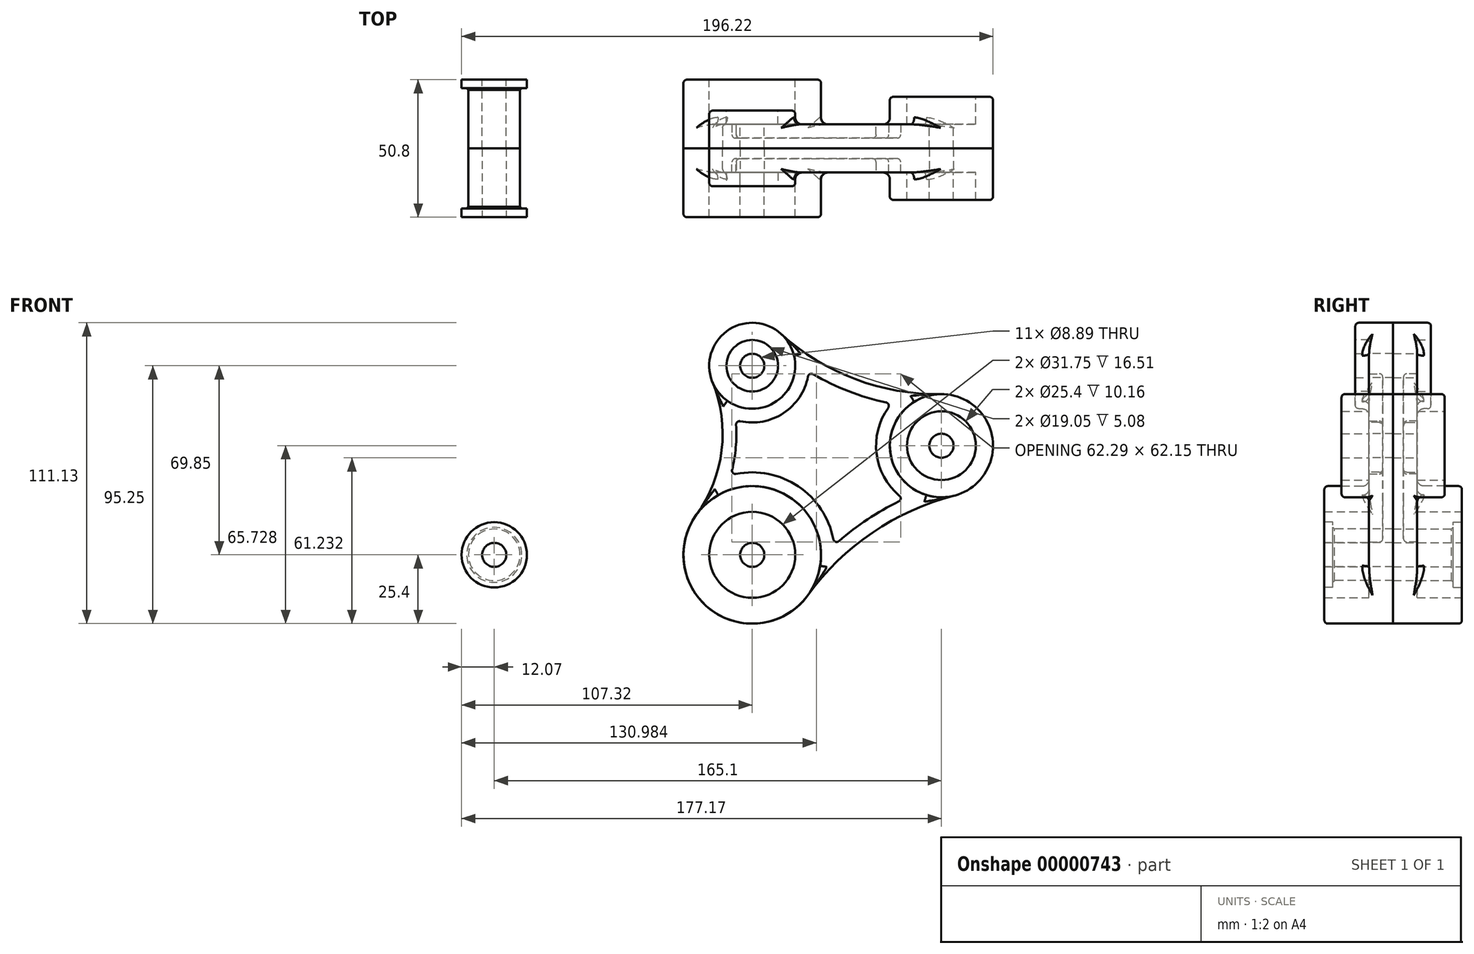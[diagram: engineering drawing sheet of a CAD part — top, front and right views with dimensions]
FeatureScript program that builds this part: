
annotation { "Feature Type Name" : "Feature", "Feature Type Description" : "" }
export const myFeature = defineFeature(function(context is Context, id is Id, definition is map)
    precondition{}
    {
        {
            var Q0;
            Q0=qCreatedBy(makeId("Front.planeOp"),FACE);
            var sketch = newSketch(context, id + "F0", { "sketchPlane" : qUnion([Q0])});
            skCircle(sketch, "E0", {"center": v(0, 0) * mm, "radius": 25.4 * mm});
            skCircle(sketch, "E1", {"center": v(0, 69.85) * mm, "radius": 15.88 * mm});
            skCircle(sketch, "E2", {"center": v(69.85, 40.33) * mm, "radius": 19.05 * mm});
            skLineSegment(sketch, "E3", {"start": v(0, 0) * mm, "end": v(69.85, 40.33) * mm, "construction": true});
            skLineSegment(sketch, "E4", {"start": v(0, 0) * mm, "end": v(74.27, 0) * mm, "construction": true});
            skArc(sketch, "E5", {"start": v(-20.58, 14.89) * mm, "mid": v(-11.3, 38.61) * mm, "end": v(-14.7, 63.85) * mm});
            skArc(sketch, "E6", {"start": v(74.6, 21.88) * mm, "mid": v(44.37, 8.2) * mm, "end": v(20.56, -14.91) * mm});
            skArc(sketch, "E7", {"start": v(10.64, 81.63) * mm, "mid": v(38.02, 64.93) * mm, "end": v(69.6, 59.38) * mm});
            skSolve(sketch);
        }
        {
            var Q0;
            {var subQ0=sQuery(id+"F0.wireOp",EDGE,"E0");var subQ1=sQuery(id+"F0.wireOp",EDGE,"E6");var subQ3=sQuery(id+"F0.wireOp",EDGE,"E5");var subQ4=makeQuery(id+"F0.imprint","INTERSECT",VERTEX,{"derivedFrom":[subQ0,subQ3]});var subQ6=sQuery(id+"F0.wireOp",EDGE,"E1");var subQ9=makeQuery(id+"F0.imprint","INTERSECT",VERTEX,{"derivedFrom":[subQ6,subQ3]});var subQ11=sQuery(id+"F0.wireOp",EDGE,"E2");var subQ13=makeQuery(id+"F0.imprint","INTERSECT",VERTEX,{"derivedFrom":[subQ11,subQ1]});var subQ14=makeQuery(id+"F0.imprint","IMPRINT",EDGE,{"disambiguationData":[TD([[subQ13,1.0]])],"derivedFrom":subQ11});Q0=qUnion([makeQuery(id+"F0.imprint","IMPRINT",FACE,{"disambiguationData":[TD([[makeQuery(id+"F0.imprint","IMPRINT",EDGE,{"disambiguationData":[TD([[subQ4,-1.0]])],"derivedFrom":subQ0}),1.0]])]}),makeQuery(id+"F0.imprint","IMPRINT",FACE,{"disambiguationData":[TD([[makeQuery(id+"F0.imprint","IMPRINT",EDGE,{"disambiguationData":[TD([[subQ9,1.0]])],"derivedFrom":subQ6}),1.0]])]}),makeQuery(id+"F0.imprint","IMPRINT",FACE,{"disambiguationData":[TD([[subQ14,1.0]])]}),makeQuery(id+"F0.imprint","IMPRINT",FACE,{"disambiguationData":[TD([[makeQuery(id+"F0.imprint","IMPRINT",EDGE,{"derivedFrom":subQ3}),-1.0]])]})]);}
            extrude(context, id + "F1", {"entities" : qUnion([Q0]), "depth" : 8.9 * mm});
        }
        {
            var Q0;
            {var subQ0=sQuery(id+"F0.wireOp",EDGE,"E1");var subQ2=makeQuery(id+"F0.imprint","INTERSECT",VERTEX,{"derivedFrom":[subQ0,sQuery(id+"F0.wireOp",EDGE,"E5")]});Q0=makeQuery(id+"F0.imprint","IMPRINT",FACE,{"disambiguationData":[TD([[makeQuery(id+"F0.imprint","IMPRINT",EDGE,{"disambiguationData":[TD([[subQ2,1.0]])],"derivedFrom":subQ0}),1.0]])]});}
            extrude(context, id + "F2", {"entities" : qUnion([Q0]), "operationType" : NewBodyOperationType.ADD, "depth" : 13.97 * mm});
        }
        {
            var Q0;
            {var subQ0=sQuery(id+"F0.wireOp",EDGE,"E2");var subQ2=makeQuery(id+"F0.imprint","INTERSECT",VERTEX,{"derivedFrom":[subQ0,sQuery(id+"F0.wireOp",EDGE,"E6")]});Q0=makeQuery(id+"F0.imprint","IMPRINT",FACE,{"disambiguationData":[TD([[makeQuery(id+"F0.imprint","IMPRINT",EDGE,{"disambiguationData":[TD([[subQ2,1.0]])],"derivedFrom":subQ0}),1.0]])]});}
            extrude(context, id + "F3", {"entities" : qUnion([Q0]), "operationType" : NewBodyOperationType.ADD, "depth" : 19.05 * mm});
        }
        {
            var Q0;
            {var subQ0=sQuery(id+"F0.wireOp",EDGE,"E0");var subQ2=makeQuery(id+"F0.imprint","INTERSECT",VERTEX,{"derivedFrom":[subQ0,sQuery(id+"F0.wireOp",EDGE,"E5")]});Q0=makeQuery(id+"F0.imprint","IMPRINT",FACE,{"disambiguationData":[TD([[makeQuery(id+"F0.imprint","IMPRINT",EDGE,{"disambiguationData":[TD([[subQ2,-1.0]])],"derivedFrom":subQ0}),1.0]])]});}
            extrude(context, id + "F4", {"entities" : qUnion([Q0]), "operationType" : NewBodyOperationType.ADD, "depth" : 25.4 * mm});
        }
        {
            var Q0;
            Q0=makeQuery(id+"F1.opExtrude","CAP_FACE",FACE,{"disambiguationData":[OSD([sQuery(id+"F0.wireOp",EDGE,"E0"),sQuery(id+"F0.wireOp",EDGE,"E1"),sQuery(id+"F0.wireOp",EDGE,"E2"),sQuery(id+"F0.wireOp",EDGE,"E5"),sQuery(id+"F0.wireOp",EDGE,"E6"),sQuery(id+"F0.wireOp",EDGE,"E7")])],"isStart":false});
            var sketch = newSketch(context, id + "F5", { "sketchPlane" : qUnion([Q0])});
            skCircle(sketch, "E8.0", {"center": v(0, 69.85) * mm, "radius": 20.96 * mm});
            skCircle(sketch, "E9.0", {"center": v(69.85, 40.33) * mm, "radius": 24.13 * mm});
            skCircle(sketch, "E10.0", {"center": v(0, 0) * mm, "radius": 30.48 * mm});
            skArc(sketch, "E11.0", {"start": v(-16.46, 11.91) * mm, "mid": v(-6.25, 38) * mm, "end": v(-10, 65.77) * mm});
            skArc(sketch, "E12.0", {"start": v(7.23, 77.86) * mm, "mid": v(36.23, 60.18) * mm, "end": v(69.67, 54.3) * mm});
            skArc(sketch, "E13.0", {"start": v(73.34, 26.8) * mm, "mid": v(41.51, 12.4) * mm, "end": v(16.45, -11.93) * mm});
            skSolve(sketch);
        }
        {
            var Q0;
            {var subQ5=sQuery(id+"F5.wireOp",EDGE,"E12.0");var subQ7=sQuery(id+"F5.wireOp",EDGE,"E8.0");var subQ8=makeQuery(id+"F5.imprint","INTERSECT",VERTEX,{"derivedFrom":[subQ7,subQ5]});Q0=makeQuery(id+"F5.imprint","IMPRINT",FACE,{"disambiguationData":[TD([[makeQuery(id+"F5.imprint","IMPRINT",EDGE,{"disambiguationData":[TD([[subQ8,1.0]])],"derivedFrom":subQ7}),-1.0]])]});}
            extrude(context, id + "F6", {"entities" : qUnion([Q0]), "operationType" : NewBodyOperationType.REMOVE, "oppositeDirection" : true, "depth" : 5.08 * mm});
        }
        {
            var Q0;
            Q0=makeQuery(id+"F4.opExtrude","CAP_FACE",FACE,{"disambiguationData":[OSD([sQuery(id+"F0.wireOp",EDGE,"E0")])],"isStart":false});
            var sketch = newSketch(context, id + "F7", { "sketchPlane" : qUnion([Q0])});
            skCircle(sketch, "E14", {"center": v(0, 0) * mm, "radius": 15.88 * mm});
            skCircle(sketch, "E15.0", {"center": v(0, 69.85) * mm, "radius": 15.88 * mm, "construction": true});
            skCircle(sketch, "E15.1", {"center": v(69.85, 40.33) * mm, "radius": 19.05 * mm, "construction": true});
            skCircle(sketch, "E16", {"center": v(0, 69.85) * mm, "radius": 9.53 * mm});
            skCircle(sketch, "E17", {"center": v(69.85, 40.33) * mm, "radius": 12.7 * mm});
            skSolve(sketch);
        }
        {
            var Q0;
            Q0=makeQuery(id+"F7.imprint","IMPRINT",FACE,{"disambiguationData":[TD([[makeQuery(id+"F7.imprint","IMPRINT",EDGE,{"derivedFrom":sQuery(id+"F7.wireOp",EDGE,"E14")}),1.0]])]});
            var Q1;
            Q1=makeQuery(id+"F7.imprint","IMPRINT",FACE,{"disambiguationData":[TD([[makeQuery(id+"F7.imprint","IMPRINT",EDGE,{"derivedFrom":sQuery(id+"F7.wireOp",EDGE,"E16")}),1.0]])]});
            var Q2;
            Q2=makeQuery(id+"F7.imprint","IMPRINT",FACE,{"disambiguationData":[TD([[makeQuery(id+"F7.imprint","IMPRINT",EDGE,{"derivedFrom":sQuery(id+"F7.wireOp",EDGE,"E17")}),1.0]])]});
            var Q3;
            Q3=makeQuery(id+"F1.opExtrude","CAP_FACE",FACE,{"disambiguationData":[OSD([sQuery(id+"F0.wireOp",EDGE,"E0"),sQuery(id+"F0.wireOp",EDGE,"E1"),sQuery(id+"F0.wireOp",EDGE,"E2"),sQuery(id+"F0.wireOp",EDGE,"E5"),sQuery(id+"F0.wireOp",EDGE,"E6"),sQuery(id+"F0.wireOp",EDGE,"E7")])],"isStart":false});
            extrude(context, id + "F8", {"entities" : qUnion([Q0, Q1, Q2]), "operationType" : NewBodyOperationType.REMOVE, "endBound" : BoundingType.UP_TO_SURFACE, "oppositeDirection" : true, "endBoundEntityFace" : qUnion([Q3]), "depth" : 25.4 * mm});
        }
        {
            var Q0;
            Q0=makeQuery(id+"F8.boolean.opBoolean","COPY",FACE,{"derivedFrom":makeQuery(id+"F8.opExtrude","CAP_FACE",FACE,{"disambiguationData":[OSD([sQuery(id+"F7.wireOp",EDGE,"E17")])],"isStart":false})});
            var sketch = newSketch(context, id + "F9", { "sketchPlane" : qUnion([Q0])});
            skCircle(sketch, "E18.0", {"center": v(0, 69.85) * mm, "radius": 9.53 * mm});
            skCircle(sketch, "E18.1", {"center": v(0, 0) * mm, "radius": 15.88 * mm});
            skCircle(sketch, "E18.2", {"center": v(69.85, 40.33) * mm, "radius": 12.7 * mm});
            skCircle(sketch, "E19", {"center": v(0, 0) * mm, "radius": 4.45 * mm});
            skCircle(sketch, "E20", {"center": v(0, 69.85) * mm, "radius": 4.45 * mm});
            skCircle(sketch, "E21", {"center": v(69.85, 40.33) * mm, "radius": 4.45 * mm});
            skSolve(sketch);
        }
        {
            var Q0;
            Q0=makeQuery(id+"F9.imprint","IMPRINT",FACE,{"disambiguationData":[TD([[makeQuery(id+"F9.imprint","IMPRINT",EDGE,{"derivedFrom":sQuery(id+"F9.wireOp",EDGE,"E20")}),1.0]])]});
            var Q1;
            Q1=makeQuery(id+"F9.imprint","IMPRINT",FACE,{"disambiguationData":[TD([[makeQuery(id+"F9.imprint","IMPRINT",EDGE,{"derivedFrom":sQuery(id+"F9.wireOp",EDGE,"E21")}),1.0]])]});
            var Q2;
            Q2=makeQuery(id+"F9.imprint","IMPRINT",FACE,{"disambiguationData":[TD([[makeQuery(id+"F9.imprint","IMPRINT",EDGE,{"derivedFrom":sQuery(id+"F9.wireOp",EDGE,"E19")}),1.0]])]});
            extrude(context, id + "F10", {"entities" : qUnion([Q0, Q1, Q2]), "operationType" : NewBodyOperationType.REMOVE, "endBound" : BoundingType.THROUGH_ALL, "oppositeDirection" : true, "depth" : 25.4 * mm});
        }
        {
            var Q0;
            Q0=makeQuery(id+"F6.boolean.opBoolean","COPY",FACE,{"derivedFrom":makeQuery(id+"F6.opExtrude","CAP_FACE",FACE,{"disambiguationData":[OSD([sQuery(id+"F5.wireOp",EDGE,"E8.0"),sQuery(id+"F5.wireOp",EDGE,"E9.0"),sQuery(id+"F5.wireOp",EDGE,"E10.0"),sQuery(id+"F5.wireOp",EDGE,"E11.0"),sQuery(id+"F5.wireOp",EDGE,"E12.0"),sQuery(id+"F5.wireOp",EDGE,"E13.0")])],"isStart":false})});
            var Q1;
            Q1=makeQuery(id+"F6.boolean.opBoolean","COPY",EDGE,{"derivedFrom":makeQuery(id+"F6.opExtrude","SWEPT_EDGE",EDGE,{"disambiguationData":[OSD([sQuery(id+"F5.wireOp",EDGE,"E8.0"),sQuery(id+"F5.wireOp",EDGE,"E11.0")])]})});
            var Q2;
            Q2=makeQuery(id+"F6.boolean.opBoolean","COPY",EDGE,{"derivedFrom":makeQuery(id+"F6.opExtrude","SWEPT_EDGE",EDGE,{"disambiguationData":[OSD([sQuery(id+"F5.wireOp",EDGE,"E8.0"),sQuery(id+"F5.wireOp",EDGE,"E12.0")])]})});
            var Q3;
            Q3=makeQuery(id+"F6.boolean.opBoolean","COPY",EDGE,{"derivedFrom":makeQuery(id+"F6.opExtrude","SWEPT_EDGE",EDGE,{"disambiguationData":[OSD([sQuery(id+"F5.wireOp",EDGE,"E9.0"),sQuery(id+"F5.wireOp",EDGE,"E12.0")])]})});
            var Q4;
            Q4=makeQuery(id+"F6.boolean.opBoolean","COPY",EDGE,{"derivedFrom":makeQuery(id+"F6.opExtrude","SWEPT_EDGE",EDGE,{"disambiguationData":[OSD([sQuery(id+"F5.wireOp",EDGE,"E9.0"),sQuery(id+"F5.wireOp",EDGE,"E13.0")])]})});
            var Q5;
            Q5=makeQuery(id+"F6.boolean.opBoolean","COPY",EDGE,{"derivedFrom":makeQuery(id+"F6.opExtrude","SWEPT_EDGE",EDGE,{"disambiguationData":[OSD([sQuery(id+"F5.wireOp",EDGE,"E10.0"),sQuery(id+"F5.wireOp",EDGE,"E13.0")])]})});
            var Q6;
            Q6=makeQuery(id+"F6.boolean.opBoolean","COPY",EDGE,{"derivedFrom":makeQuery(id+"F6.opExtrude","SWEPT_EDGE",EDGE,{"disambiguationData":[OSD([sQuery(id+"F5.wireOp",EDGE,"E10.0"),sQuery(id+"F5.wireOp",EDGE,"E11.0")])]})});
            var Q7;
            Q7=makeQuery(id+"F6.boolean.opBoolean","COPY",EDGE,{"derivedFrom":makeQuery(id+"F6.opExtrude","CAP_EDGE",EDGE,{"disambiguationData":[OSD([sQuery(id+"F5.wireOp",EDGE,"E10.0")])],"isStart":true})});
            var Q8;
            Q8=makeQuery(id+"F1.opExtrude","CAP_EDGE",EDGE,{"disambiguationData":[OSD([sQuery(id+"F0.wireOp",EDGE,"E7")])],"isStart":false});
            var Q9;
            Q9=makeQuery(id+"F1.opExtrude","CAP_EDGE",EDGE,{"disambiguationData":[OSD([sQuery(id+"F0.wireOp",EDGE,"E6")])],"isStart":false});
            var Q10;
            Q10=makeQuery(id+"F1.opExtrude","CAP_EDGE",EDGE,{"disambiguationData":[OSD([sQuery(id+"F0.wireOp",EDGE,"E5")])],"isStart":false});
            var Q11;
            Q11=makeQuery(id+"F4.opExtrude","CAP_EDGE",EDGE,{"disambiguationData":[OSD([sQuery(id+"F0.wireOp",EDGE,"E0")])],"isStart":false});
            var Q12;
            Q12=makeQuery(id+"F3.opExtrude","CAP_EDGE",EDGE,{"disambiguationData":[OSD([sQuery(id+"F0.wireOp",EDGE,"E2")])],"isStart":false});
            var Q13;
            Q13=makeQuery(id+"F2.opExtrude","CAP_EDGE",EDGE,{"disambiguationData":[OSD([sQuery(id+"F0.wireOp",EDGE,"E1")])],"isStart":false});
            fillet(context, id + "F11", {"entities" : qUnion([Q0, Q1, Q2, Q3, Q4, Q5, Q6, Q7, Q8, Q9, Q10, Q11, Q12, Q13]), "radius" : 1.27 * mm, "tangentPropagation" : true, "allowEdgeOverflow" : false});
        }
        {
            var Q0;
            {var subQ0=sQuery(id+"F0.wireOp",EDGE,"E2");Q0=makeQuery(id+"F3.boolean.opBoolean","INTERSECT",EDGE,{"derivedFrom":[makeQuery(id+"F1.opExtrude","CAP_FACE",FACE,{"disambiguationData":[OSD([sQuery(id+"F0.wireOp",EDGE,"E0"),sQuery(id+"F0.wireOp",EDGE,"E1"),subQ0,sQuery(id+"F0.wireOp",EDGE,"E5"),sQuery(id+"F0.wireOp",EDGE,"E6"),sQuery(id+"F0.wireOp",EDGE,"E7")])],"isStart":false}),makeQuery(id+"F3.opExtrude","SWEPT_FACE",FACE,{"disambiguationData":[OSD([subQ0])]})]});}
            var Q1;
            {var subQ0=sQuery(id+"F0.wireOp",EDGE,"E0");Q1=makeQuery(id+"F4.boolean.opBoolean","INTERSECT",EDGE,{"derivedFrom":[makeQuery(id+"F1.opExtrude","CAP_FACE",FACE,{"disambiguationData":[OSD([subQ0,sQuery(id+"F0.wireOp",EDGE,"E1"),sQuery(id+"F0.wireOp",EDGE,"E2"),sQuery(id+"F0.wireOp",EDGE,"E5"),sQuery(id+"F0.wireOp",EDGE,"E6"),sQuery(id+"F0.wireOp",EDGE,"E7")])],"isStart":false}),makeQuery(id+"F4.opExtrude","SWEPT_FACE",FACE,{"disambiguationData":[OSD([subQ0])]})]});}
            var Q2;
            {var subQ0=sQuery(id+"F0.wireOp",EDGE,"E1");Q2=makeQuery(id+"F2.boolean.opBoolean","INTERSECT",EDGE,{"derivedFrom":[makeQuery(id+"F1.opExtrude","CAP_FACE",FACE,{"disambiguationData":[OSD([sQuery(id+"F0.wireOp",EDGE,"E0"),subQ0,sQuery(id+"F0.wireOp",EDGE,"E2"),sQuery(id+"F0.wireOp",EDGE,"E5"),sQuery(id+"F0.wireOp",EDGE,"E6"),sQuery(id+"F0.wireOp",EDGE,"E7")])],"isStart":false}),makeQuery(id+"F2.opExtrude","SWEPT_FACE",FACE,{"disambiguationData":[OSD([subQ0])]})]});}
            fillet(context, id + "F12", {"entities" : qUnion([Q0, Q1, Q2]), "radius" : 2.54 * mm, "tangentPropagation" : true, "allowEdgeOverflow" : false});
        }
        {
            var Q0;
            Q0=makeQuery(id+"F1.opExtrude","SWEPT_BODY",BODY,{"disambiguationData":[OSD([sQuery(id+"F0.wireOp",EDGE,"E0"),sQuery(id+"F0.wireOp",EDGE,"E1"),sQuery(id+"F0.wireOp",EDGE,"E2"),sQuery(id+"F0.wireOp",EDGE,"E5"),sQuery(id+"F0.wireOp",EDGE,"E6"),sQuery(id+"F0.wireOp",EDGE,"E7")])]});
            var Q1;
            Q1=qCreatedBy(makeId("Front.planeOp"),FACE);
            mirror(context, id + "F13", {"entities" : qUnion([Q0]), "mirrorPlane" : qUnion([Q1])});
        }
        {
            var Q0;
            Q0=makeQuery(id+"F8.boolean.opBoolean","COPY",FACE,{"derivedFrom":makeQuery(id+"F8.opExtrude","CAP_FACE",FACE,{"disambiguationData":[OSD([sQuery(id+"F7.wireOp",EDGE,"E16")])],"isStart":false})});
            var sketch = newSketch(context, id + "F14", { "sketchPlane" : qUnion([Q0])});
            skCircle(sketch, "E22.0.0", {"center": v(0, 69.85) * mm, "radius": 9.53 * mm});
            skSolve(sketch);
        }
        {
            var Q0;
            Q0=makeQuery(id+"F14.imprint","IMPRINT",FACE,{"disambiguationData":[TD([[makeQuery(id+"F14.imprint","IMPRINT",EDGE,{"derivedFrom":sQuery(id+"F14.wireOp",EDGE,"E22.0.0")}),-1.0]])]});
            var Q1;
            Q1=makeQuery(id+"F2.opExtrude","CAP_FACE",FACE,{"disambiguationData":[OSD([sQuery(id+"F0.wireOp",EDGE,"E1")])],"isStart":false});
            extrude(context, id + "F15", {"entities" : qUnion([Q0]), "endBound" : BoundingType.UP_TO_SURFACE, "endBoundEntityFace" : qUnion([Q1]), "depth" : 25.4 * mm});
        }
        {
            var Q0;
            Q0=makeQuery(id+"F8.boolean.opBoolean","COPY",FACE,{"derivedFrom":makeQuery(id+"F8.opExtrude","CAP_FACE",FACE,{"disambiguationData":[OSD([sQuery(id+"F7.wireOp",EDGE,"E17")])],"isStart":false})});
            var Q1;
            Q1=makeQuery(id+"F3.opExtrude","CAP_FACE",FACE,{"disambiguationData":[OSD([sQuery(id+"F0.wireOp",EDGE,"E2")])],"isStart":false});
            extrude(context, id + "F16", {"entities" : qUnion([Q0]), "endBound" : BoundingType.UP_TO_SURFACE, "endBoundEntityFace" : qUnion([Q1]), "depth" : 25.4 * mm});
        }
        {
            var Q0;
            Q0=makeQuery(id+"F8.boolean.opBoolean","COPY",FACE,{"derivedFrom":makeQuery(id+"F8.opExtrude","CAP_FACE",FACE,{"disambiguationData":[OSD([sQuery(id+"F7.wireOp",EDGE,"E14")])],"isStart":false})});
            var sketch = newSketch(context, id + "F17", { "sketchPlane" : qUnion([Q0])});
            skCircle(sketch, "E23.0", {"center": v(0, 0) * mm, "radius": 4.45 * mm});
            skCircle(sketch, "E23.1", {"center": v(0, 0) * mm, "radius": 15.88 * mm});
            skSolve(sketch);
        }
        {
            var Q0;
            Q0=makeQuery(id+"F17.imprint","IMPRINT",FACE,{"disambiguationData":[TD([[makeQuery(id+"F17.imprint","IMPRINT",EDGE,{"derivedFrom":sQuery(id+"F17.wireOp",EDGE,"E23.0")}),-1.0]])]});
            var Q1;
            Q1=makeQuery(id+"F4.opExtrude","CAP_FACE",FACE,{"disambiguationData":[OSD([sQuery(id+"F0.wireOp",EDGE,"E0")])],"isStart":false});
            extrude(context, id + "F18", {"entities" : qUnion([Q0]), "endBound" : BoundingType.UP_TO_SURFACE, "endBoundEntityFace" : qUnion([Q1]), "depth" : 25.4 * mm});
        }
        {
            var Q0;
            Q0=qCreatedBy(makeId("Top.planeOp"),FACE);
            var sketch = newSketch(context, id + "F19", { "sketchPlane" : qUnion([Q0])});
            skLineSegment(sketch, "E24", {"start": v(-90.8, 0) * mm, "end": v(-90.8, -25.4) * mm});
            skLineSegment(sketch, "E25", {"start": v(-90.8, -25.4) * mm, "end": v(-83.19, -25.4) * mm});
            skLineSegment(sketch, "E26", {"start": v(-83.19, -25.4) * mm, "end": v(-83.19, -22.23) * mm});
            skLineSegment(sketch, "E27", {"start": v(-83.19, -22.23) * mm, "end": v(-85.1, -22.23) * mm});
            skLineSegment(sketch, "E28", {"start": v(-85.1, -22.23) * mm, "end": v(-85.73, -21.6) * mm});
            skLineSegment(sketch, "E29", {"start": v(-85.73, -21.6) * mm, "end": v(-85.73, 0) * mm});
            skLineSegment(sketch, "E30", {"start": v(-85.73, 0) * mm, "end": v(-90.8, 0) * mm});
            skLineSegment(sketch, "E31.0", {"start": v(24.13, -25.4) * mm, "end": v(-24.13, -25.4) * mm});
            skLineSegment(sketch, "E32", {"start": v(-95.25, -25.4) * mm, "end": v(-95.25, 0) * mm, "construction": true});
            skSolve(sketch);
        }
        {
            var Q0;
            Q0=makeQuery(id+"F19.imprint","IMPRINT",FACE,{"disambiguationData":[TD([[makeQuery(id+"F19.imprint","IMPRINT",EDGE,{"derivedFrom":sQuery(id+"F19.wireOp",EDGE,"E24")}),1.0]])]});
            var Q1;
            Q1=sQuery(id+"F19.wireOp",EDGE,"E32");
            revolve(context, id + "F20", {"entities" : qUnion([Q0]), "axis" : qUnion([Q1]), "revolveType" : RevolveType.FULL});
        }
        {
            var Q0;
            Q0=makeQuery(id+"F20.opRevolve","SWEPT_BODY",BODY,{"disambiguationData":[OSD([sQuery(id+"F19.wireOp",EDGE,"E24"),sQuery(id+"F19.wireOp",EDGE,"E25"),sQuery(id+"F19.wireOp",EDGE,"E26"),sQuery(id+"F19.wireOp",EDGE,"E27"),sQuery(id+"F19.wireOp",EDGE,"E28"),sQuery(id+"F19.wireOp",EDGE,"E29"),sQuery(id+"F19.wireOp",EDGE,"E30")])]});
            var Q1;
            Q1=makeQuery(id+"F20.opRevolve","SWEPT_FACE",FACE,{"disambiguationData":[OSD([sQuery(id+"F19.wireOp",EDGE,"E30")])]});
            mirror(context, id + "F21", {"entities" : qUnion([Q0]), "mirrorPlane" : qUnion([Q1])});
        }
    });
